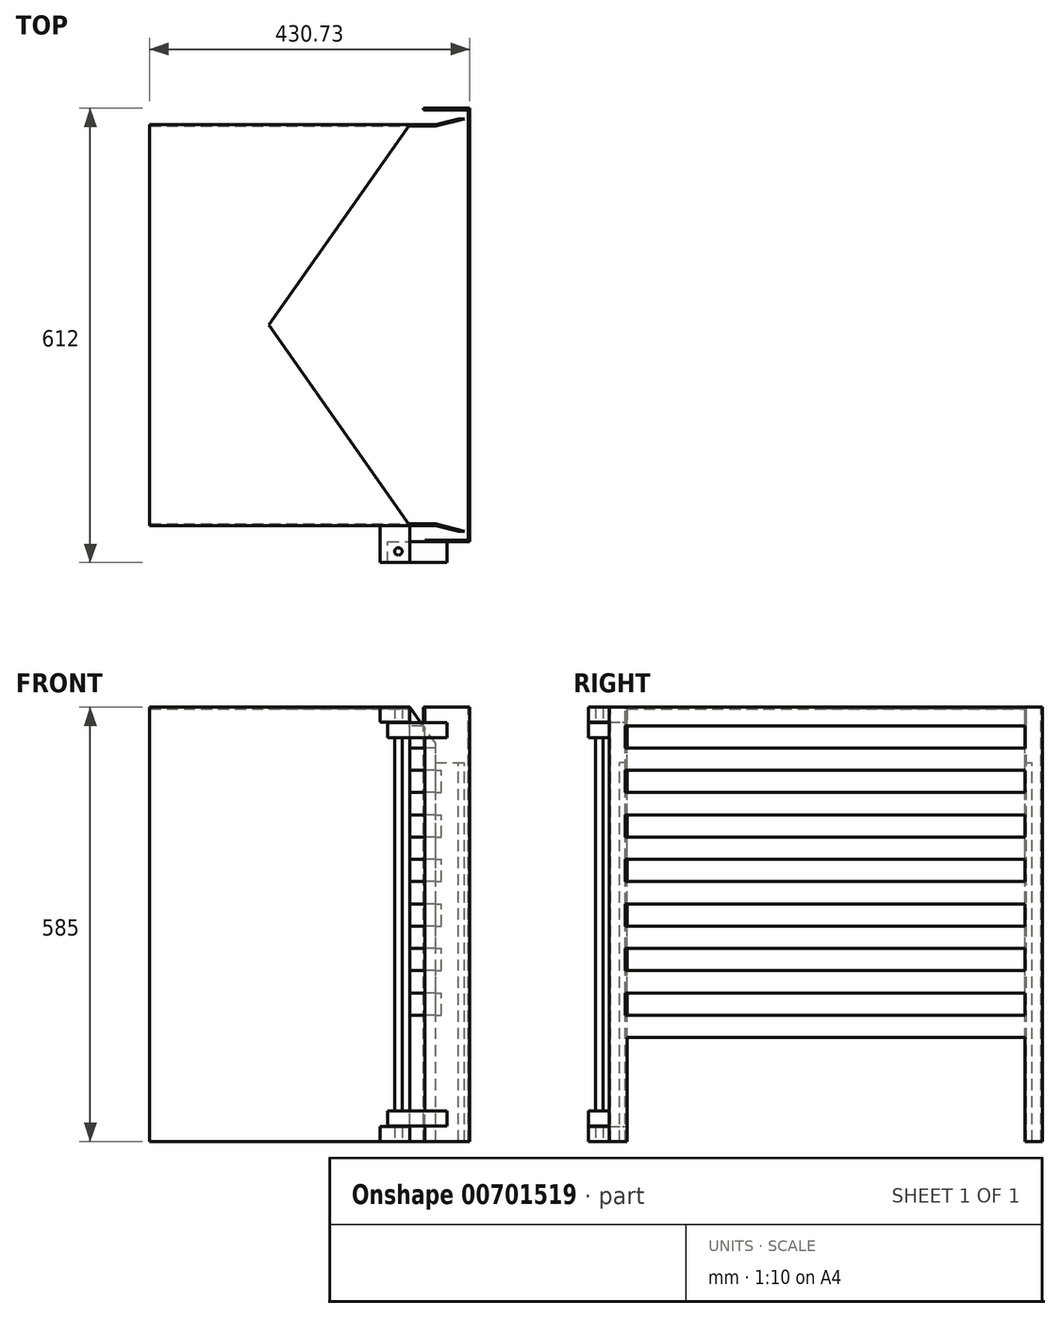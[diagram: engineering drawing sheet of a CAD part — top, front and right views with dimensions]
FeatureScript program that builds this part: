
annotation { "Feature Type Name" : "Feature", "Feature Type Description" : "" }
export const myFeature = defineFeature(function(context is Context, id is Id, definition is map)
    precondition{}
    {
        {
            var Q0;
            Q0=qCreatedBy(makeId("Right.planeOp"),FACE);
            var sketch = newSketch(context, id + "F0", { "sketchPlane" : qUnion([Q0])});
            skLineSegment(sketch, "E0.bottom", {"start": v(0, 0) * mm, "end": v(540, 0) * mm});
            skLineSegment(sketch, "E0.top", {"start": v(0, 585) * mm, "end": v(540, 585) * mm});
            skLineSegment(sketch, "E0.left", {"start": v(0, 0) * mm, "end": v(0, 585) * mm});
            skLineSegment(sketch, "E0.right", {"start": v(540, 0) * mm, "end": v(540, 585) * mm});
            skSolve(sketch);
        }
        {
            var Q0;
            Q0 = qSketchRegion(id + "F0", true);
            extrude(context, id + "F1", {"entities" : qUnion([Q0]), "oppositeDirection" : true, "depth" : 350 * mm, "offsetDistance" : 25 * mm});
        }
        {
            var Q0;
            Q0=makeQuery(id+"F1.opExtrude","CAP_FACE",FACE,{"disambiguationData":[OSD([sQuery(id+"F0.wireOp",EDGE,"E0.bottom"),sQuery(id+"F0.wireOp",EDGE,"E0.top"),sQuery(id+"F0.wireOp",EDGE,"E0.left"),sQuery(id+"F0.wireOp",EDGE,"E0.right")])],"isStart":true});
            var sketch = newSketch(context, id + "F2", { "sketchPlane" : qUnion([Q0])});
            skLineSegment(sketch, "E1.bottom", {"start": v(2, 0) * mm, "end": v(538, 0) * mm});
            skLineSegment(sketch, "E1.top", {"start": v(2, 583) * mm, "end": v(538, 583) * mm});
            skLineSegment(sketch, "E1.left", {"start": v(2, 0) * mm, "end": v(2, 583) * mm});
            skLineSegment(sketch, "E1.right", {"start": v(538, 0) * mm, "end": v(538, 583) * mm});
            skSolve(sketch);
        }
        {
            var Q0;
            Q0 = qSketchRegion(id + "F2", true);
            extrude(context, id + "F3", {"entities" : qUnion([Q0]), "operationType" : NewBodyOperationType.REMOVE, "oppositeDirection" : true, "depth" : 350 * mm, "offsetDistance" : 25 * mm});
        }
        {
            var Q0;
            Q0=makeQuery(id+"F1.opExtrude","SWEPT_FACE",FACE,{"disambiguationData":[OSD([sQuery(id+"F0.wireOp",EDGE,"E0.top")])]});
            var sketch = newSketch(context, id + "F4", { "sketchPlane" : qUnion([Q0])});
            skLineSegment(sketch, "E2", {"start": v(0, 0) * mm, "end": v(-189.74, 270) * mm});
            skLineSegment(sketch, "E3", {"start": v(-189.74, 270) * mm, "end": v(0, 540) * mm});
            skLineSegment(sketch, "E4", {"start": v(0, 540) * mm, "end": v(0, 0) * mm});
            skSolve(sketch);
        }
        {
            var Q0;
            Q0 = qSketchRegion(id + "F4", true);
            extrude(context, id + "F5", {"entities" : qUnion([Q0]), "operationType" : NewBodyOperationType.REMOVE, "oppositeDirection" : true, "depth" : 25 * mm, "offsetDistance" : 25 * mm});
        }
        {
            var Q0;
            Q0=makeQuery(id+"F1.opExtrude","SWEPT_FACE",FACE,{"disambiguationData":[OSD([sQuery(id+"F0.wireOp",EDGE,"E0.left")])]});
            var sketch = newSketch(context, id + "F6", { "sketchPlane" : qUnion([Q0])});
            skLineSegment(sketch, "E5", {"start": v(0, 0) * mm, "end": v(35, 0) * mm});
            skLineSegment(sketch, "E6", {"start": v(35, 0) * mm, "end": v(35, 536.27) * mm});
            skLineSegment(sketch, "E7", {"start": v(35, 536.27) * mm, "end": v(0, 585) * mm});
            skLineSegment(sketch, "E8", {"start": v(0, 585) * mm, "end": v(0, 0) * mm});
            skSolve(sketch);
        }
        {
            var Q0;
            Q0 = qSketchRegion(id + "F6", true);
            extrude(context, id + "F7", {"entities" : qUnion([Q0]), "oppositeDirection" : true, "depth" : 540 * mm, "offsetDistance" : 25 * mm});
        }
        {
            var Q0;
            Q0=makeQuery(id+"F7.opExtrude","SWEPT_FACE",FACE,{"disambiguationData":[OSD([sQuery(id+"F6.wireOp",EDGE,"E6")])]});
            var sketch = newSketch(context, id + "F8", { "sketchPlane" : qUnion([Q0])});
            skLineSegment(sketch, "E9.bottom", {"start": v(2, 0) * mm, "end": v(538, 0) * mm});
            skLineSegment(sketch, "E9.top", {"start": v(2, 585) * mm, "end": v(538, 585) * mm});
            skLineSegment(sketch, "E9.left", {"start": v(2, 0) * mm, "end": v(2, 585) * mm});
            skLineSegment(sketch, "E9.right", {"start": v(538, 0) * mm, "end": v(538, 585) * mm});
            skSolve(sketch);
        }
        {
            var Q0;
            Q0 = qSketchRegion(id + "F8", true);
            extrude(context, id + "F9", {"entities" : qUnion([Q0]), "operationType" : NewBodyOperationType.REMOVE, "oppositeDirection" : true, "depth" : 35 * mm, "offsetDistance" : 25 * mm});
        }
        {
            var Q0;
            Q0=qCreatedBy(makeId("Top.planeOp"),FACE);
            cPlane(context, id + "F10", {"entities" : qUnion([Q0]), "cplaneType" : CPlaneType.OFFSET, "offset" : (585 - 75) * mm, "width" : 150 * mm, "height" : 150 * mm});
        }
        {
            var Q0;
            Q0=qCreatedBy(id+"F10.planeOp",FACE);
            var sketch = newSketch(context, id + "F11", { "sketchPlane" : qUnion([Q0])});
            skLineSegment(sketch, "E10", {"start": v(0, 0) * mm, "end": v(61.52, 0) * mm, "construction": true});
            skLineSegment(sketch, "E11", {"start": v(-3.42, 2) * mm, "end": v(56.54, 2) * mm, "construction": true});
            skLineSegment(sketch, "E12", {"start": v(35, -13.23) * mm, "end": v(35, 21.51) * mm, "construction": true});
            skLineSegment(sketch, "E13", {"start": v(35, 0) * mm, "end": v(65.98, -8) * mm});
            skLineSegment(sketch, "E14", {"start": v(35, 2) * mm, "end": v(73.73, -8) * mm});
            skLineSegment(sketch, "E15", {"start": v(65.98, -8) * mm, "end": v(73.73, -8) * mm});
            skLineSegment(sketch, "E16", {"start": v(35, 2) * mm, "end": v(35, 0) * mm});
            skLineSegment(sketch, "E17", {"start": v(35, 554.08) * mm, "end": v(35, 523.78) * mm, "construction": true});
            skLineSegment(sketch, "E18", {"start": v(0, 540) * mm, "end": v(49.53, 540) * mm, "construction": true});
            skLineSegment(sketch, "E19", {"start": v(0, 538) * mm, "end": v(51.42, 538) * mm, "construction": true});
            skLineSegment(sketch, "E20", {"start": v(35, 540) * mm, "end": v(65.98, 548) * mm});
            skLineSegment(sketch, "E21", {"start": v(35, 538) * mm, "end": v(73.73, 548) * mm});
            skLineSegment(sketch, "E22", {"start": v(73.73, 548) * mm, "end": v(65.98, 548) * mm});
            skLineSegment(sketch, "E23", {"start": v(35, 540) * mm, "end": v(35, 538) * mm});
            skSolve(sketch);
        }
        {
            var Q0;
            Q0 = qSketchRegion(id + "F11", true);
            extrude(context, id + "F12", {"entities" : qUnion([Q0]), "oppositeDirection" : true, "depth" : (585 - 75) * mm, "offsetDistance" : 25 * mm});
        }
        {
            var Q0;
            Q0=qCreatedBy(makeId("Top.planeOp"),FACE);
            cPlane(context, id + "F13", {"entities" : qUnion([Q0]), "cplaneType" : CPlaneType.OFFSET, "offset" : 585 * mm, "width" : 150 * mm, "height" : 150 * mm});
        }
        {
            var Q0;
            Q0=qCreatedBy(id+"F13.planeOp",FACE);
            var sketch = newSketch(context, id + "F14", { "sketchPlane" : qUnion([Q0])});
            skLineSegment(sketch, "E24", {"start": v(-59.42, 540) * mm, "end": v(102.8, 540) * mm, "construction": true});
            skLineSegment(sketch, "E25", {"start": v(0, 540) * mm, "end": v(-35, 540) * mm});
            skLineSegment(sketch, "E26", {"start": v(35, 19.41) * mm, "end": v(35, -17.91) * mm, "construction": true});
            skLineSegment(sketch, "E27", {"start": v(35, 0) * mm, "end": v(35, -2.07) * mm});
            skLineSegment(sketch, "E28", {"start": v(20.73, -20) * mm, "end": v(78.73, -20) * mm});
            skLineSegment(sketch, "E29", {"start": v(20.73, -20) * mm, "end": v(20.73, -22) * mm});
            skLineSegment(sketch, "E30", {"start": v(20.73, -22) * mm, "end": v(80.73, -22) * mm});
            skLineSegment(sketch, "E31", {"start": v(18.73, 560) * mm, "end": v(78.73, 560) * mm});
            skLineSegment(sketch, "E32", {"start": v(18.73, 562) * mm, "end": v(80.73, 562) * mm});
            skLineSegment(sketch, "E33", {"start": v(18.73, 562) * mm, "end": v(18.73, 560) * mm});
            skLineSegment(sketch, "E34", {"start": v(78.73, -20) * mm, "end": v(78.73, 560) * mm});
            skLineSegment(sketch, "E35", {"start": v(80.73, 562) * mm, "end": v(80.73, -22) * mm});
            skSolve(sketch);
        }
        {
            var Q0;
            Q0 = qSketchRegion(id + "F14", true);
            extrude(context, id + "F15", {"entities" : qUnion([Q0]), "oppositeDirection" : true, "depth" : 585 * mm, "offsetDistance" : 25 * mm});
        }
        {
            var Q0;
            Q0=qCreatedBy(makeId("Right.planeOp"),FACE);
            var sketch = newSketch(context, id + "F16", { "sketchPlane" : qUnion([Q0])});
            skLineSegment(sketch, "E36", {"start": v(2, 5.15) * mm, "end": v(2, -1.65) * mm, "construction": true});
            skLineSegment(sketch, "E37.bottom", {"start": v(2, 0) * mm, "end": v(538, 0) * mm});
            skLineSegment(sketch, "E37.top", {"start": v(2, 140) * mm, "end": v(538, 140) * mm});
            skLineSegment(sketch, "E37.left", {"start": v(2, 0) * mm, "end": v(2, 140) * mm});
            skLineSegment(sketch, "E37.right", {"start": v(538, 0) * mm, "end": v(538, 140) * mm});
            skLineSegment(sketch, "E38.bottom", {"start": v(538, 170) * mm, "end": v(0, 170) * mm});
            skLineSegment(sketch, "E38.top", {"start": v(538, 200) * mm, "end": v(0, 200) * mm});
            skLineSegment(sketch, "E38.left", {"start": v(538, 170) * mm, "end": v(538, 200) * mm});
            skLineSegment(sketch, "E38.right", {"start": v(0, 170) * mm, "end": v(0, 200) * mm});
            skPoint(sketch, "E39.oppositeSnap0", {"position": v(0, 185) * mm});
            skLineSegment(sketch, "E39.bottom", {"start": v(538, 230) * mm, "end": v(0, 230) * mm});
            skLineSegment(sketch, "E39.top", {"start": v(538, 260) * mm, "end": v(0, 260) * mm});
            skLineSegment(sketch, "E39.left", {"start": v(538, 230) * mm, "end": v(538, 260) * mm});
            skLineSegment(sketch, "E39.right", {"start": v(0, 230) * mm, "end": v(0, 260) * mm});
            skLineSegment(sketch, "E40.bottom", {"start": v(538, 290) * mm, "end": v(0, 290) * mm});
            skLineSegment(sketch, "E40.top", {"start": v(538, 320) * mm, "end": v(0, 320) * mm});
            skLineSegment(sketch, "E40.left", {"start": v(538, 290) * mm, "end": v(538, 320) * mm});
            skLineSegment(sketch, "E40.right", {"start": v(0, 290) * mm, "end": v(0, 320) * mm});
            skLineSegment(sketch, "E41.bottom", {"start": v(538, 350) * mm, "end": v(0, 350) * mm});
            skLineSegment(sketch, "E41.top", {"start": v(538, 380) * mm, "end": v(0, 380) * mm});
            skLineSegment(sketch, "E41.left", {"start": v(538, 350) * mm, "end": v(538, 380) * mm});
            skLineSegment(sketch, "E41.right", {"start": v(0, 350) * mm, "end": v(0, 380) * mm});
            skLineSegment(sketch, "E42.bottom", {"start": v(538, 530) * mm, "end": v(0, 530) * mm});
            skLineSegment(sketch, "E42.top", {"start": v(538, 560) * mm, "end": v(0, 560) * mm});
            skLineSegment(sketch, "E42.left", {"start": v(538, 530) * mm, "end": v(538, 560) * mm});
            skLineSegment(sketch, "E42.right", {"start": v(0, 530) * mm, "end": v(0, 560) * mm});
            skLineSegment(sketch, "E43.bottom", {"start": v(538, 470) * mm, "end": v(0, 470) * mm});
            skLineSegment(sketch, "E43.top", {"start": v(538, 500) * mm, "end": v(0, 500) * mm});
            skLineSegment(sketch, "E43.left", {"start": v(538, 470) * mm, "end": v(538, 500) * mm});
            skLineSegment(sketch, "E43.right", {"start": v(0, 470) * mm, "end": v(0, 500) * mm});
            skLineSegment(sketch, "E44.bottom", {"start": v(538, 410) * mm, "end": v(0, 410) * mm});
            skLineSegment(sketch, "E44.top", {"start": v(538, 440) * mm, "end": v(0, 440) * mm});
            skLineSegment(sketch, "E44.left", {"start": v(538, 410) * mm, "end": v(538, 440) * mm});
            skLineSegment(sketch, "E44.right", {"start": v(0, 410) * mm, "end": v(0, 440) * mm});
            skSolve(sketch);
        }
        {
            var Q0;
            Q0 = qSketchRegion(id + "F16", true);
            extrude(context, id + "F17", {"entities" : qUnion([Q0]), "operationType" : NewBodyOperationType.REMOVE, "depth" : 100 * mm, "offsetDistance" : 25 * mm});
        }
        {
            var Q0;
            Q0=qCreatedBy(makeId("Front.planeOp"),FACE);
            var sketch = newSketch(context, id + "F18", { "sketchPlane" : qUnion([Q0])});
            skLineSegment(sketch, "E45.bottom", {"start": v(0, 0) * mm, "end": v(-40, 0) * mm});
            skLineSegment(sketch, "E45.top", {"start": v(0, 20) * mm, "end": v(-40, 20) * mm});
            skLineSegment(sketch, "E45.left", {"start": v(0, 0) * mm, "end": v(0, 20) * mm});
            skLineSegment(sketch, "E45.right", {"start": v(-40, 0) * mm, "end": v(-40, 20) * mm});
            skLineSegment(sketch, "E46.bottom", {"start": v(0, 565) * mm, "end": v(-40, 565) * mm});
            skLineSegment(sketch, "E46.top", {"start": v(0, 585) * mm, "end": v(-40, 585) * mm});
            skLineSegment(sketch, "E46.left", {"start": v(0, 565) * mm, "end": v(0, 585) * mm});
            skLineSegment(sketch, "E46.right", {"start": v(-40, 565) * mm, "end": v(-40, 585) * mm});
            skSolve(sketch);
        }
        {
            var Q0;
            Q0 = qSketchRegion(id + "F18", true);
            extrude(context, id + "F19", {"entities" : qUnion([Q0]), "depth" : 50 * mm, "offsetDistance" : 25 * mm});
        }
        {
            var Q0;
            Q0=qCreatedBy(makeId("Top.planeOp"),FACE);
            var sketch = newSketch(context, id + "F20", { "sketchPlane" : qUnion([Q0])});
            skCircle(sketch, "E47", {"center": v(-15, -35) * mm, "radius": 5 * mm});
            skSolve(sketch);
        }
        {
            var Q0;
            Q0 = qSketchRegion(id + "F20", true);
            extrude(context, id + "F21", {"entities" : qUnion([Q0]), "depth" : 585 * mm, "offsetDistance" : 25 * mm});
        }
        {
            var Q0;
            Q0=makeQuery(id+"F15.opExtrude","SWEPT_FACE",FACE,{"disambiguationData":[OSD([sQuery(id+"F14.wireOp",EDGE,"E30")])]});
            var sketch = newSketch(context, id + "F22", { "sketchPlane" : qUnion([Q0])});
            skLineSegment(sketch, "E48.bottom", {"start": v(-29.27, 564) * mm, "end": v(50.73, 564) * mm});
            skLineSegment(sketch, "E48.top", {"start": v(-29.27, 544) * mm, "end": v(50.73, 544) * mm});
            skLineSegment(sketch, "E48.left", {"start": v(-29.27, 564) * mm, "end": v(-29.27, 544) * mm});
            skLineSegment(sketch, "E48.right", {"start": v(50.73, 564) * mm, "end": v(50.73, 544) * mm});
            skLineSegment(sketch, "E49.bottom", {"start": v(-29.27, 21) * mm, "end": v(50.73, 21) * mm});
            skLineSegment(sketch, "E49.top", {"start": v(-29.27, 41) * mm, "end": v(50.73, 41) * mm});
            skLineSegment(sketch, "E49.left", {"start": v(-29.27, 21) * mm, "end": v(-29.27, 41) * mm});
            skLineSegment(sketch, "E49.right", {"start": v(50.73, 21) * mm, "end": v(50.73, 41) * mm});
            skSolve(sketch);
        }
        {
            var Q0;
            Q0 = qSketchRegion(id + "F22", true);
            extrude(context, id + "F23", {"entities" : qUnion([Q0]), "operationType" : NewBodyOperationType.ADD, "depth" : 28 * mm, "offsetDistance" : 25 * mm});
        }
    });
